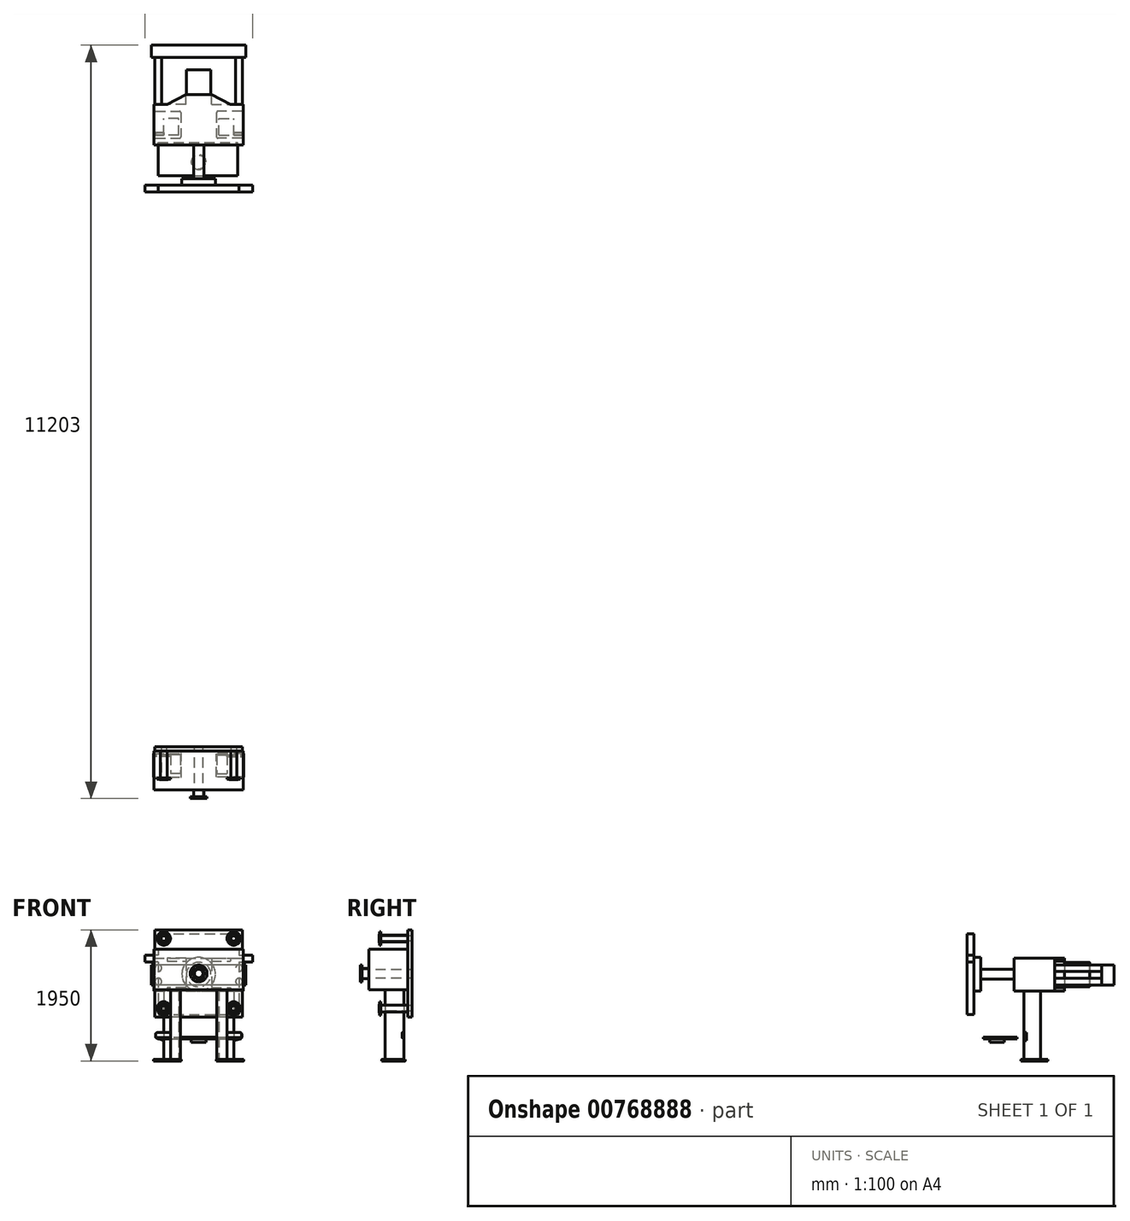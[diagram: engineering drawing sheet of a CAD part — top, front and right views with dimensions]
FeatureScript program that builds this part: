
annotation { "Feature Type Name" : "Feature", "Feature Type Description" : "" }
export const myFeature = defineFeature(function(context is Context, id is Id, definition is map)
    precondition{}
    {
        {
            var Q0;
            Q0=qCreatedBy(makeId("Top.planeOp"),FACE);
            var sketch = newSketch(context, id + "F0", { "sketchPlane" : qUnion([Q0])});
            skLineSegment(sketch, "E0.bottom", {"start": v(-645, 200) * mm, "end": v(-285, 200) * mm});
            skLineSegment(sketch, "E0.top", {"start": v(-645, -200) * mm, "end": v(-285, -200) * mm});
            skLineSegment(sketch, "E0.left", {"start": v(-665, 180) * mm, "end": v(-665, -180) * mm});
            skLineSegment(sketch, "E0.right", {"start": v(-265, 180) * mm, "end": v(-265, -180) * mm});
            skPoint(sketch, "E0.middle", {"position": v(-465, 0) * mm});
            skPoint(sketch, "E1.visualSharp", {"position": v(-665, 200) * mm});
            skArc(sketch, "E1.filletArc", {"start": v(-645, 200) * mm, "mid": v(-659.14, 194.14) * mm, "end": v(-665, 180) * mm});
            skPoint(sketch, "E2.visualSharp", {"position": v(-265, 200) * mm});
            skArc(sketch, "E2.filletArc", {"start": v(-265, 180) * mm, "mid": v(-270.86, 194.14) * mm, "end": v(-285, 200) * mm});
            skPoint(sketch, "E3.visualSharp", {"position": v(-265, -200) * mm});
            skArc(sketch, "E3.filletArc", {"start": v(-285, -200) * mm, "mid": v(-270.86, -194.14) * mm, "end": v(-265, -180) * mm});
            skPoint(sketch, "E4.visualSharp", {"position": v(-665, -200) * mm});
            skArc(sketch, "E4.filletArc", {"start": v(-665, -180) * mm, "mid": v(-659.14, -194.14) * mm, "end": v(-645, -200) * mm});
            skArc(sketch, "E5.MirrorCS", {"start": v(265, 180) * mm, "mid": v(270.86, 194.14) * mm, "end": v(285, 200) * mm});
            skArc(sketch, "E6.MirrorCS", {"start": v(285, -200) * mm, "mid": v(270.86, -194.14) * mm, "end": v(265, -180) * mm});
            skArc(sketch, "E7.MirrorCS", {"start": v(645, 200) * mm, "mid": v(659.14, 194.14) * mm, "end": v(665, 180) * mm});
            skArc(sketch, "E8.MirrorCS", {"start": v(665, -180) * mm, "mid": v(659.14, -194.14) * mm, "end": v(645, -200) * mm});
            skPoint(sketch, "E9.MirrorP", {"position": v(665, -200) * mm});
            skLineSegment(sketch, "E10.MirrorCS", {"start": v(265, 180) * mm, "end": v(265, -180) * mm});
            skPoint(sketch, "E11.MirrorP", {"position": v(665, 200) * mm});
            skPoint(sketch, "E12.MirrorP", {"position": v(265, 200) * mm});
            skLineSegment(sketch, "E13.MirrorCS", {"start": v(665, 180) * mm, "end": v(665, -180) * mm});
            skPoint(sketch, "E14.MirrorP", {"position": v(465, 0) * mm});
            skLineSegment(sketch, "E15.MirrorCS", {"start": v(645, -200) * mm, "end": v(285, -200) * mm});
            skLineSegment(sketch, "E16.MirrorCS", {"start": v(645, 200) * mm, "end": v(285, 200) * mm});
            skPoint(sketch, "E17.MirrorP", {"position": v(265, -200) * mm});
            skSolve(sketch);
        }
        {
            var Q0;
            Q0=makeQuery(id+"F0.imprint","IMPRINT",FACE,{"disambiguationData":[TD([[makeQuery(id+"F0.imprint","IMPRINT",EDGE,{"derivedFrom":sQuery(id+"F0.wireOp",EDGE,"E0.bottom")}),-1.0]])]});
            var sketch = newSketch(context, id + "F1", { "sketchPlane" : qUnion([Q0])});
            skPoint(sketch, "E18.0", {"position": v(-465, 0) * mm});
            skLineSegment(sketch, "E19.bottom", {"start": v(-665, -9700) * mm, "end": v(-265, -9700) * mm});
            skLineSegment(sketch, "E19.top", {"start": v(-665, -9350) * mm, "end": v(-265, -9350) * mm});
            skLineSegment(sketch, "E19.left", {"start": v(-670, -9695) * mm, "end": v(-670, -9355) * mm});
            skLineSegment(sketch, "E19.right", {"start": v(-260, -9695) * mm, "end": v(-260, -9355) * mm});
            skPoint(sketch, "E19.middle", {"position": v(-465, -9525) * mm});
            skPoint(sketch, "E20.visualSharp", {"position": v(-670, -9350) * mm});
            skArc(sketch, "E20.filletArc", {"start": v(-665, -9350) * mm, "mid": v(-668.54, -9351.46) * mm, "end": v(-670, -9355) * mm});
            skPoint(sketch, "E21.visualSharp", {"position": v(-670, -9700) * mm});
            skArc(sketch, "E21.filletArc", {"start": v(-670, -9695) * mm, "mid": v(-668.54, -9698.54) * mm, "end": v(-665, -9700) * mm});
            skPoint(sketch, "E22.visualSharp", {"position": v(-260, -9350) * mm});
            skArc(sketch, "E22.filletArc", {"start": v(-260, -9355) * mm, "mid": v(-261.46, -9351.46) * mm, "end": v(-265, -9350) * mm});
            skPoint(sketch, "E23.visualSharp", {"position": v(-260, -9700) * mm});
            skArc(sketch, "E23.filletArc", {"start": v(-265, -9700) * mm, "mid": v(-261.46, -9698.54) * mm, "end": v(-260, -9695) * mm});
            skArc(sketch, "E24.MirrorCS", {"start": v(260, -9355) * mm, "mid": v(261.46, -9351.46) * mm, "end": v(265, -9350) * mm});
            skArc(sketch, "E25.MirrorCS", {"start": v(670, -9695) * mm, "mid": v(668.54, -9698.54) * mm, "end": v(665, -9700) * mm});
            skArc(sketch, "E26.MirrorCS", {"start": v(265, -9700) * mm, "mid": v(261.46, -9698.54) * mm, "end": v(260, -9695) * mm});
            skArc(sketch, "E27.MirrorCS", {"start": v(665, -9350) * mm, "mid": v(668.54, -9351.46) * mm, "end": v(670, -9355) * mm});
            skLineSegment(sketch, "E28.MirrorCS", {"start": v(670, -9695) * mm, "end": v(670, -9355) * mm});
            skLineSegment(sketch, "E29.MirrorCS", {"start": v(260, -9695) * mm, "end": v(260, -9355) * mm});
            skLineSegment(sketch, "E30.MirrorCS", {"start": v(665, -9350) * mm, "end": v(265, -9350) * mm});
            skLineSegment(sketch, "E31.MirrorCS", {"start": v(665, -9700) * mm, "end": v(265, -9700) * mm});
            skPoint(sketch, "E32.MirrorP", {"position": v(670, -9350) * mm});
            skPoint(sketch, "E33.MirrorP", {"position": v(670, -9700) * mm});
            skPoint(sketch, "E34.MirrorP", {"position": v(260, -9700) * mm});
            skPoint(sketch, "E35.MirrorP", {"position": v(260, -9350) * mm});
            skPoint(sketch, "E36.MirrorP", {"position": v(465, -9525) * mm});
            skSolve(sketch);
        }
        {
            var Q0;
            Q0 = qSketchRegion(id + "F0", true);
            var Q1;
            Q1 = qSketchRegion(id + "F1", true);
            extrude(context, id + "F2", {"entities" : qUnion([Q0, Q1]), "depth" : 20 * mm, "offsetDistance" : 25 * mm});
        }
        {
            var Q0;
            Q0=makeQuery(id+"F2.opExtrude","CAP_FACE",FACE,{"disambiguationData":[OSD([sQuery(id+"F0.wireOp",EDGE,"E0.bottom"),sQuery(id+"F0.wireOp",EDGE,"E0.top"),sQuery(id+"F0.wireOp",EDGE,"E0.left"),sQuery(id+"F0.wireOp",EDGE,"E0.right"),sQuery(id+"F0.wireOp",EDGE,"E1.filletArc"),sQuery(id+"F0.wireOp",EDGE,"E2.filletArc"),sQuery(id+"F0.wireOp",EDGE,"E3.filletArc"),sQuery(id+"F0.wireOp",EDGE,"E4.filletArc")])],"isStart":false});
            var sketch = newSketch(context, id + "F3", { "sketchPlane" : qUnion([Q0])});
            skLineSegment(sketch, "E37.bottom", {"start": v(-300, -156.09) * mm, "end": v(-520, -156.09) * mm});
            skLineSegment(sketch, "E37.top", {"start": v(-300, 93.91) * mm, "end": v(-520, 93.91) * mm});
            skLineSegment(sketch, "E37.left", {"start": v(-300, -156.09) * mm, "end": v(-300, 93.91) * mm});
            skLineSegment(sketch, "E37.right", {"start": v(-520, -156.09) * mm, "end": v(-520, 93.91) * mm});
            skPoint(sketch, "E37.middle", {"position": v(-410, -31.09) * mm});
            skLineSegment(sketch, "E38.MirrorCS", {"start": v(300, -156.09) * mm, "end": v(520, -156.09) * mm});
            skLineSegment(sketch, "E39.MirrorCS", {"start": v(300, 93.91) * mm, "end": v(520, 93.91) * mm});
            skLineSegment(sketch, "E40.MirrorCS", {"start": v(520, -156.09) * mm, "end": v(520, 93.91) * mm});
            skLineSegment(sketch, "E41.MirrorCS", {"start": v(300, -156.09) * mm, "end": v(300, 93.91) * mm});
            skPoint(sketch, "E42.MirrorP", {"position": v(410, -31.09) * mm});
            skSolve(sketch);
        }
        {
            var Q0;
            Q0 = qSketchRegion(id + "F3", true);
            extrude(context, id + "F4", {"entities" : qUnion([Q0]), "operationType" : NewBodyOperationType.ADD, "depth" : 1020 * mm, "offsetDistance" : 25 * mm});
        }
        {
            var Q0;
            Q0=makeQuery(id+"F2.opExtrude","CAP_FACE",FACE,{"disambiguationData":[OSD([sQuery(id+"F1.wireOp",EDGE,"E19.bottom"),sQuery(id+"F1.wireOp",EDGE,"E19.top"),sQuery(id+"F1.wireOp",EDGE,"E19.left"),sQuery(id+"F1.wireOp",EDGE,"E19.right"),sQuery(id+"F1.wireOp",EDGE,"E20.filletArc"),sQuery(id+"F1.wireOp",EDGE,"E21.filletArc"),sQuery(id+"F1.wireOp",EDGE,"E22.filletArc"),sQuery(id+"F1.wireOp",EDGE,"E23.filletArc")])],"isStart":false});
            var sketch = newSketch(context, id + "F5", { "sketchPlane" : qUnion([Q0])});
            skLineSegment(sketch, "E43.bottom", {"start": v(-270, -9370) * mm, "end": v(-420, -9370) * mm});
            skLineSegment(sketch, "E43.top", {"start": v(-270, -9650) * mm, "end": v(-420, -9650) * mm});
            skLineSegment(sketch, "E43.left", {"start": v(-270, -9370) * mm, "end": v(-270, -9650) * mm});
            skLineSegment(sketch, "E43.right", {"start": v(-420, -9370) * mm, "end": v(-420, -9650) * mm});
            skLineSegment(sketch, "E44.MirrorCS", {"start": v(270, -9370) * mm, "end": v(420, -9370) * mm});
            skLineSegment(sketch, "E45.MirrorCS", {"start": v(420, -9370) * mm, "end": v(420, -9650) * mm});
            skLineSegment(sketch, "E46.MirrorCS", {"start": v(270, -9650) * mm, "end": v(420, -9650) * mm});
            skLineSegment(sketch, "E47.MirrorCS", {"start": v(270, -9370) * mm, "end": v(270, -9650) * mm});
            skSolve(sketch);
        }
        {
            var Q0;
            Q0 = qSketchRegion(id + "F5", true);
            extrude(context, id + "F6", {"entities" : qUnion([Q0]), "operationType" : NewBodyOperationType.ADD, "depth" : 1040 * mm, "offsetDistance" : 25 * mm});
        }
        {
            var Q0;
            Q0=makeQuery(id+"F4.opExtrude","CAP_FACE",FACE,{"disambiguationData":[OSD([sQuery(id+"F3.wireOp",EDGE,"E37.bottom"),sQuery(id+"F3.wireOp",EDGE,"E37.top"),sQuery(id+"F3.wireOp",EDGE,"E37.left"),sQuery(id+"F3.wireOp",EDGE,"E37.right")])],"isStart":false});
            var sketch = newSketch(context, id + "F7", { "sketchPlane" : qUnion([Q0])});
            skLineSegment(sketch, "E48.bottom", {"start": v(-663.5, 300) * mm, "end": v(-470, 300) * mm});
            skLineSegment(sketch, "E48.top", {"start": v(-663.5, -300) * mm, "end": v(663.5, -300) * mm});
            skLineSegment(sketch, "E48.left", {"start": v(-663.5, 300) * mm, "end": v(-663.5, -300) * mm});
            skLineSegment(sketch, "E48.right", {"start": v(663.5, 300) * mm, "end": v(663.5, -300) * mm});
            skLineSegment(sketch, "E49", {"start": v(-190, 450) * mm, "end": v(190, 450) * mm});
            skLineSegment(sketch, "E50", {"start": v(-190, 450) * mm, "end": v(-470, 300) * mm});
            skLineSegment(sketch, "E51", {"start": v(190, 450) * mm, "end": v(470, 300) * mm});
            skLineSegment(sketch, "E52.trimOffspring", {"start": v(470, 300) * mm, "end": v(663.5, 300) * mm});
            skSolve(sketch);
        }
        {
            var Q0;
            Q0=makeQuery(id+"F7.imprint","IMPRINT",FACE,{"disambiguationData":[TD([[makeQuery(id+"F7.imprint","IMPRINT",EDGE,{"derivedFrom":sQuery(id+"F7.wireOp",EDGE,"E48.bottom")}),-1.0]])]});
            var Q1;
            Q1=makeQuery(id+"F7.imprint","IMPRINT",FACE,{"disambiguationData":[TD([[makeQuery(id+"F7.imprint","IMPRINT",EDGE,{"derivedFrom":makeQuery(id+"F4.opExtrude","CAP_EDGE",EDGE,{"disambiguationData":[OSD([sQuery(id+"F3.wireOp",EDGE,"E37.bottom")])],"isStart":false})}),-1.0]])]});
            extrude(context, id + "F8", {"entities" : qUnion([Q0, Q1]), "operationType" : NewBodyOperationType.ADD, "depth" : 490 * mm, "offsetDistance" : 25 * mm});
        }
        {
            var Q0;
            Q0=makeQuery(id+"F6.opExtrude","CAP_FACE",FACE,{"disambiguationData":[OSD([sQuery(id+"F5.wireOp",EDGE,"E43.bottom"),sQuery(id+"F5.wireOp",EDGE,"E43.top"),sQuery(id+"F5.wireOp",EDGE,"E43.left"),sQuery(id+"F5.wireOp",EDGE,"E43.right")])],"isStart":false});
            var sketch = newSketch(context, id + "F9", { "sketchPlane" : qUnion([Q0])});
            skLineSegment(sketch, "E53.bottom", {"start": v(-663.5, -9310) * mm, "end": v(663.5, -9310) * mm});
            skLineSegment(sketch, "E53.top", {"start": v(-663.5, -9889) * mm, "end": v(663.5, -9889) * mm});
            skLineSegment(sketch, "E53.left", {"start": v(-663.5, -9310) * mm, "end": v(-663.5, -9889) * mm});
            skLineSegment(sketch, "E53.right", {"start": v(663.5, -9310) * mm, "end": v(663.5, -9889) * mm});
            skSolve(sketch);
        }
        {
            var Q0;
            Q0=makeQuery(id+"F9.imprint","IMPRINT",FACE,{"disambiguationData":[TD([[makeQuery(id+"F9.imprint","IMPRINT",EDGE,{"derivedFrom":sQuery(id+"F9.wireOp",EDGE,"E53.bottom")}),-1.0]])]});
            var Q1;
            Q1=makeQuery(id+"F9.imprint","IMPRINT",FACE,{"disambiguationData":[TD([[makeQuery(id+"F9.imprint","IMPRINT",EDGE,{"derivedFrom":makeQuery(id+"F6.opExtrude","CAP_EDGE",EDGE,{"disambiguationData":[OSD([sQuery(id+"F5.wireOp",EDGE,"E43.bottom")])],"isStart":false})}),1.0]])]});
            extrude(context, id + "F10", {"entities" : qUnion([Q0, Q1]), "operationType" : NewBodyOperationType.ADD, "depth" : 600 * mm, "offsetDistance" : 25 * mm});
        }
        {
            var Q0;
            Q0=makeQuery(id+"F8.opExtrude","SWEPT_FACE",FACE,{"disambiguationData":[OSD([sQuery(id+"F7.wireOp",EDGE,"E49")])]});
            var sketch = newSketch(context, id + "F11", { "sketchPlane" : qUnion([Q0])});
            skCircle(sketch, "E54", {"center": v(0, 1285) * mm, "radius": 182 * mm});
            skSolve(sketch);
        }
        {
            var Q0;
            Q0=makeQuery(id+"F11.imprint","IMPRINT",FACE,{"disambiguationData":[TD([[makeQuery(id+"F11.imprint","IMPRINT",EDGE,{"derivedFrom":sQuery(id+"F11.wireOp",EDGE,"E54")}),1.0]])]});
            extrude(context, id + "F12", {"entities" : qUnion([Q0]), "operationType" : NewBodyOperationType.ADD, "depth" : 370 * mm, "offsetDistance" : 25 * mm});
        }
        {
            var Q0;
            Q0=makeQuery(id+"F8.opExtrude","SWEPT_FACE",FACE,{"disambiguationData":[OSD([sQuery(id+"F7.wireOp",EDGE,"E49")])]});
            var sketch = newSketch(context, id + "F13", { "sketchPlane" : qUnion([Q0])});
            skLineSegment(sketch, "E55.bottom", {"start": v(-190, 1484.67) * mm, "end": v(-470, 1484.67) * mm});
            skLineSegment(sketch, "E55.top", {"start": v(-190, 1087.5) * mm, "end": v(-470, 1087.5) * mm});
            skLineSegment(sketch, "E55.left", {"start": v(-190, 1484.67) * mm, "end": v(-190, 1087.5) * mm});
            skLineSegment(sketch, "E55.right", {"start": v(-470, 1484.67) * mm, "end": v(-470, 1087.5) * mm});
            skLineSegment(sketch, "E56.bottom", {"start": v(190, 1484.67) * mm, "end": v(470, 1484.67) * mm});
            skLineSegment(sketch, "E56.top", {"start": v(190, 1087.5) * mm, "end": v(470, 1087.5) * mm});
            skLineSegment(sketch, "E56.left", {"start": v(190, 1484.67) * mm, "end": v(190, 1087.5) * mm});
            skLineSegment(sketch, "E56.right", {"start": v(470, 1484.67) * mm, "end": v(470, 1087.5) * mm});
            skSolve(sketch);
        }
        {
            var Q0;
            Q0=makeQuery(id+"F13.imprint","IMPRINT",FACE,{"disambiguationData":[TD([[makeQuery(id+"F13.imprint","IMPRINT",EDGE,{"derivedFrom":sQuery(id+"F13.wireOp",EDGE,"E55.bottom")}),1.0]])]});
            var Q1;
            Q1=makeQuery(id+"F13.imprint","IMPRINT",FACE,{"disambiguationData":[TD([[makeQuery(id+"F13.imprint","IMPRINT",EDGE,{"derivedFrom":sQuery(id+"F13.wireOp",EDGE,"E56.bottom")}),-1.0]])]});
            extrude(context, id + "F14", {"entities" : qUnion([Q0, Q1]), "operationType" : NewBodyOperationType.REMOVE, "oppositeDirection" : true, "depth" : 150 * mm, "offsetDistance" : 25 * mm});
        }
        {
            var Q0;
            Q0=makeQuery(id+"F10.opExtrude","SWEPT_FACE",FACE,{"disambiguationData":[OSD([sQuery(id+"F9.wireOp",EDGE,"E53.bottom")])]});
            var sketch = newSketch(context, id + "F15", { "sketchPlane" : qUnion([Q0])});
            skLineSegment(sketch, "E57.bottom", {"start": v(-650, 1950) * mm, "end": v(650, 1950) * mm});
            skLineSegment(sketch, "E57.top", {"start": v(-650, 650) * mm, "end": v(650, 650) * mm});
            skLineSegment(sketch, "E57.left", {"start": v(-650, 1950) * mm, "end": v(-650, 650) * mm});
            skLineSegment(sketch, "E57.right", {"start": v(650, 1950) * mm, "end": v(650, 650) * mm});
            skSolve(sketch);
        }
        {
            var Q0;
            Q0 = qSketchRegion(id + "F15", true);
            extrude(context, id + "F16", {"entities" : qUnion([Q0]), "operationType" : NewBodyOperationType.ADD, "depth" : 60 * mm, "offsetDistance" : 25 * mm});
        }
        {
            var Q0;
            Q0=makeQuery(id+"F8.opExtrude","SWEPT_FACE",FACE,{"disambiguationData":[OSD([sQuery(id+"F7.wireOp",EDGE,"E48.top")])]});
            var sketch = newSketch(context, id + "F17", { "sketchPlane" : qUnion([Q0])});
            skCircle(sketch, "E58", {"center": v(0, 1290) * mm, "radius": 75 * mm});
            skSolve(sketch);
        }
        {
            var Q0;
            Q0=makeQuery(id+"F17.imprint","IMPRINT",FACE,{"disambiguationData":[TD([[makeQuery(id+"F17.imprint","IMPRINT",EDGE,{"derivedFrom":sQuery(id+"F17.wireOp",EDGE,"E58")}),1.0]])]});
            extrude(context, id + "F18", {"entities" : qUnion([Q0]), "depth" : 600 * mm, "offsetDistance" : 25 * mm});
        }
        {
            var Q0;
            Q0=makeQuery(id+"F18.opExtrude","CAP_FACE",FACE,{"disambiguationData":[OSD([sQuery(id+"F17.wireOp",EDGE,"E58")])],"isStart":false});
            var sketch = newSketch(context, id + "F19", { "sketchPlane" : qUnion([Q0])});
            skLineSegment(sketch, "E59.bottom", {"start": v(-600, 1890) * mm, "end": v(600, 1890) * mm});
            skLineSegment(sketch, "E59.top", {"start": v(-600, 690) * mm, "end": v(600, 690) * mm});
            skLineSegment(sketch, "E59.left", {"start": v(-600, 1890) * mm, "end": v(-600, 1570) * mm});
            skLineSegment(sketch, "E59.right", {"start": v(600, 1890) * mm, "end": v(600, 1570) * mm});
            skPoint(sketch, "E59.middle", {"position": v(0, 1290) * mm});
            skLineSegment(sketch, "E60.bottom", {"start": v(-600, 1570) * mm, "end": v(-800, 1570) * mm});
            skLineSegment(sketch, "E60.top", {"start": v(-600, 1470) * mm, "end": v(-800, 1470) * mm});
            skLineSegment(sketch, "E60.right", {"start": v(-800, 1570) * mm, "end": v(-800, 1470) * mm});
            skLineSegment(sketch, "E61.bottom", {"start": v(600, 1470) * mm, "end": v(800, 1470) * mm});
            skLineSegment(sketch, "E61.top", {"start": v(600, 1570) * mm, "end": v(800, 1570) * mm});
            skLineSegment(sketch, "E61.right", {"start": v(800, 1470) * mm, "end": v(800, 1570) * mm});
            skLineSegment(sketch, "E62.trimOffspring", {"start": v(-600, 1470) * mm, "end": v(-600, 690) * mm});
            skLineSegment(sketch, "E63.trimOffspring", {"start": v(600, 1470) * mm, "end": v(600, 690) * mm});
            skSolve(sketch);
        }
        {
            var Q0;
            Q0=makeQuery(id+"F19.imprint","IMPRINT",FACE,{"disambiguationData":[TD([[makeQuery(id+"F19.imprint","IMPRINT",EDGE,{"derivedFrom":sQuery(id+"F19.wireOp",EDGE,"E59.bottom")}),-1.0]])]});
            var Q1;
            Q1=makeQuery(id+"F19.imprint","IMPRINT",FACE,{"disambiguationData":[TD([[makeQuery(id+"F19.imprint","IMPRINT",EDGE,{"derivedFrom":makeQuery(id+"F18.opExtrude","CAP_EDGE",EDGE,{"disambiguationData":[OSD([sQuery(id+"F17.wireOp",EDGE,"E58")])],"isStart":false})}),1.0]])]});
            extrude(context, id + "F20", {"entities" : qUnion([Q0, Q1]), "operationType" : NewBodyOperationType.ADD, "depth" : 100 * mm, "offsetDistance" : 25 * mm});
        }
        {
            var Q0;
            Q0=makeQuery(id+"F20.opExtrude","CAP_FACE",FACE,{"disambiguationData":[OSD([sQuery(id+"F19.wireOp",EDGE,"E59.bottom"),sQuery(id+"F19.wireOp",EDGE,"E59.top"),sQuery(id+"F19.wireOp",EDGE,"E59.left"),sQuery(id+"F19.wireOp",EDGE,"E59.right"),sQuery(id+"F19.wireOp",EDGE,"E60.bottom"),sQuery(id+"F19.wireOp",EDGE,"E60.top"),sQuery(id+"F19.wireOp",EDGE,"E60.right"),sQuery(id+"F19.wireOp",EDGE,"E61.bottom"),sQuery(id+"F19.wireOp",EDGE,"E61.top"),sQuery(id+"F19.wireOp",EDGE,"E61.right"),sQuery(id+"F19.wireOp",EDGE,"E62.trimOffspring"),sQuery(id+"F19.wireOp",EDGE,"E63.trimOffspring")])],"isStart":true});
            var sketch = newSketch(context, id + "F21", { "sketchPlane" : qUnion([Q0])});
            skCircle(sketch, "E64", {"center": v(0, 1290) * mm, "radius": 250 * mm});
            skSolve(sketch);
        }
        {
            var Q0;
            Q0=makeQuery(id+"F21.imprint","IMPRINT",FACE,{"disambiguationData":[TD([[makeQuery(id+"F21.imprint","IMPRINT",EDGE,{"derivedFrom":sQuery(id+"F21.wireOp",EDGE,"E64")}),1.0]])]});
            extrude(context, id + "F22", {"entities" : qUnion([Q0]), "operationType" : NewBodyOperationType.ADD, "depth" : 100 * mm, "offsetDistance" : 25 * mm});
        }
        {
            var Q0;
            {var subQ0=sQuery(id+"F15.wireOp",EDGE,"E57.left");var subQ1=sQuery(id+"F15.wireOp",EDGE,"E57.bottom");var subQ3=sQuery(id+"F15.wireOp",EDGE,"E57.right");Q0=makeQuery(id+"F16.boolean.opBoolean","SPLIT",FACE,{"disambiguationData":[TD([makeQuery(id+"F16.opExtrude","SWEPT_FACE",FACE,{"disambiguationData":[OSD([subQ1])]})])],"derivedFrom":makeQuery(id+"F16.opExtrude","CAP_FACE",FACE,{"disambiguationData":[OSD([subQ1,sQuery(id+"F15.wireOp",EDGE,"E57.top"),subQ0,subQ3])],"isStart":true})});}
            var sketch = newSketch(context, id + "F23", { "sketchPlane" : qUnion([Q0])});
            skCircle(sketch, "E65", {"center": v(-520, 1820) * mm, "radius": 40 * mm});
            skCircle(sketch, "E66", {"center": v(520, 1820) * mm, "radius": 40 * mm});
            skSolve(sketch);
        }
        {
            var Q0;
            Q0 = qSketchRegion(id + "F23", true);
            extrude(context, id + "F24", {"entities" : qUnion([Q0]), "operationType" : NewBodyOperationType.REMOVE, "oppositeDirection" : true, "depth" : 60 * mm, "offsetDistance" : 25 * mm});
        }
        {
            var Q0;
            {var subQ0=sQuery(id+"F15.wireOp",EDGE,"E57.left");var subQ1=sQuery(id+"F15.wireOp",EDGE,"E57.bottom");var subQ3=sQuery(id+"F15.wireOp",EDGE,"E57.right");Q0=makeQuery(id+"F16.boolean.opBoolean","SPLIT",FACE,{"disambiguationData":[TD([makeQuery(id+"F16.opExtrude","SWEPT_FACE",FACE,{"disambiguationData":[OSD([subQ1])]})])],"derivedFrom":makeQuery(id+"F16.opExtrude","CAP_FACE",FACE,{"disambiguationData":[OSD([subQ1,sQuery(id+"F15.wireOp",EDGE,"E57.top"),subQ0,subQ3])],"isStart":true})});}
            var sketch = newSketch(context, id + "F25", { "sketchPlane" : qUnion([Q0])});
            skCircle(sketch, "E67", {"center": v(-520, 1820) * mm, "radius": 50 * mm});
            skCircle(sketch, "E68", {"center": v(-520, 1820) * mm, "radius": 100 * mm});
            skCircle(sketch, "E69", {"center": v(-440, 1820) * mm, "radius": 9 * mm});
            skCircle(sketch, "E70.1.0", {"center": v(-463.43, 1876.57) * mm, "radius": 9 * mm});
            skCircle(sketch, "E70.2.0", {"center": v(-520, 1900) * mm, "radius": 9 * mm});
            skCircle(sketch, "E70.3.0", {"center": v(-576.57, 1876.57) * mm, "radius": 9 * mm});
            skCircle(sketch, "E70.4.0", {"center": v(-600, 1820) * mm, "radius": 9 * mm});
            skCircle(sketch, "E70.5.0", {"center": v(-576.57, 1763.43) * mm, "radius": 9 * mm});
            skCircle(sketch, "E70.6.0", {"center": v(-520, 1740) * mm, "radius": 9 * mm});
            skCircle(sketch, "E70.7.0", {"center": v(-463.43, 1763.43) * mm, "radius": 9 * mm});
            skSolve(sketch);
        }
        {
            var Q0;
            Q0=makeQuery(id+"F25.imprint","IMPRINT",FACE,{"disambiguationData":[TD([[makeQuery(id+"F25.imprint","IMPRINT",EDGE,{"derivedFrom":sQuery(id+"F25.wireOp",EDGE,"E67")}),1.0]])]});
            extrude(context, id + "F26", {"entities" : qUnion([Q0]), "operationType" : NewBodyOperationType.ADD, "depth" : 420 * mm, "offsetDistance" : 25 * mm});
        }
        {
            var Q0;
            Q0=makeQuery(id+"F26.opExtrude","CAP_FACE",FACE,{"disambiguationData":[OSD([sQuery(id+"F23.wireOp",EDGE,"E65"),sQuery(id+"F25.wireOp",EDGE,"E67")])],"isStart":false});
            var sketch = newSketch(context, id + "F27", { "sketchPlane" : qUnion([Q0])});
            skCircle(sketch, "E71.0", {"center": v(-520, 1900) * mm, "radius": 9 * mm});
            skCircle(sketch, "E71.1", {"center": v(-576.57, 1876.57) * mm, "radius": 9 * mm});
            skCircle(sketch, "E72.0", {"center": v(-463.43, 1763.43) * mm, "radius": 9 * mm});
            skCircle(sketch, "E72.1", {"center": v(-520, 1820) * mm, "radius": 50 * mm});
            skCircle(sketch, "E72.2", {"center": v(-520, 1820) * mm, "radius": 100 * mm});
            skCircle(sketch, "E72.3", {"center": v(-440, 1820) * mm, "radius": 9 * mm});
            skCircle(sketch, "E72.4", {"center": v(-463.43, 1876.57) * mm, "radius": 9 * mm});
            skCircle(sketch, "E72.7", {"center": v(-576.57, 1763.43) * mm, "radius": 9 * mm});
            skCircle(sketch, "E72.8", {"center": v(-520, 1820) * mm, "radius": 50 * mm});
            skCircle(sketch, "E72.9", {"center": v(-520, 1820) * mm, "radius": 40 * mm});
            skLineSegment(sketch, "E72.10", {"start": v(-663.5, 1530) * mm, "end": v(-663.5, 1040) * mm});
            skCircle(sketch, "E73.4", {"center": v(-600, 1820) * mm, "radius": 9 * mm});
            skCircle(sketch, "E73.6", {"center": v(-520, 1740) * mm, "radius": 9 * mm});
            skSolve(sketch);
        }
        {
            var Q0;
            Q0=makeQuery(id+"F27.imprint","IMPRINT",FACE,{"disambiguationData":[TD([[makeQuery(id+"F27.imprint","IMPRINT",EDGE,{"derivedFrom":sQuery(id+"F27.wireOp",EDGE,"E72.4")}),-1.0]])]});
            extrude(context, id + "F28", {"entities" : qUnion([Q0]), "operationType" : NewBodyOperationType.ADD, "oppositeDirection" : true, "depth" : 20 * mm, "offsetDistance" : 25 * mm});
        }
        {
            var Q0;
            Q0=makeQuery(id+"F28.boolean.opBoolean","MERGE",FACE,{"derivedFrom":[makeQuery(id+"F26.opExtrude","CAP_FACE",FACE,{"disambiguationData":[OSD([sQuery(id+"F23.wireOp",EDGE,"E65"),sQuery(id+"F25.wireOp",EDGE,"E67")])],"isStart":false}),makeQuery(id+"F28.opExtrude","CAP_FACE",FACE,{"disambiguationData":[OSD([sQuery(id+"F27.wireOp",EDGE,"E72.4"),sQuery(id+"F27.wireOp",EDGE,"E71.0"),sQuery(id+"F27.wireOp",EDGE,"E71.1"),sQuery(id+"F27.wireOp",EDGE,"E72.0"),sQuery(id+"F27.wireOp",EDGE,"E72.1"),sQuery(id+"F27.wireOp",EDGE,"E72.2"),sQuery(id+"F27.wireOp",EDGE,"E72.3"),sQuery(id+"F27.wireOp",EDGE,"E73.4"),sQuery(id+"F27.wireOp",EDGE,"E72.7"),sQuery(id+"F27.wireOp",EDGE,"E73.6")])],"isStart":true})]});
            var sketch = newSketch(context, id + "F29", { "sketchPlane" : qUnion([Q0])});
            skCircle(sketch, "E74", {"center": v(-520, 1820) * mm, "radius": 65 * mm});
            skSolve(sketch);
        }
        {
            var Q0;
            Q0=makeQuery(id+"F29.imprint","IMPRINT",FACE,{"disambiguationData":[TD([[makeQuery(id+"F29.imprint","IMPRINT",EDGE,{"derivedFrom":sQuery(id+"F29.wireOp",EDGE,"E74")}),1.0]])]});
            extrude(context, id + "F30", {"entities" : qUnion([Q0]), "operationType" : NewBodyOperationType.ADD, "depth" : 5 * mm, "offsetDistance" : 25 * mm});
        }
        {
            var Q0;
            Q0=makeQuery(id+"F25.imprint","IMPRINT",FACE,{"disambiguationData":[TD([[makeQuery(id+"F25.imprint","IMPRINT",EDGE,{"derivedFrom":sQuery(id+"F25.wireOp",EDGE,"E68")}),-1.0]])]});
            var sketch = newSketch(context, id + "F31", { "sketchPlane" : qUnion([Q0])});
            skCircle(sketch, "E75.0", {"center": v(520, 1820) * mm, "radius": 40 * mm});
            skCircle(sketch, "E76", {"center": v(520, 1820) * mm, "radius": 45 * mm});
            skCircle(sketch, "E77", {"center": v(520, 1820) * mm, "radius": 100 * mm});
            skCircle(sketch, "E78", {"center": v(600, 1820) * mm, "radius": 9 * mm});
            skCircle(sketch, "E79.1.0", {"center": v(576.57, 1876.57) * mm, "radius": 9 * mm});
            skCircle(sketch, "E79.2.0", {"center": v(520, 1900) * mm, "radius": 9 * mm});
            skCircle(sketch, "E79.3.0", {"center": v(463.43, 1876.57) * mm, "radius": 9 * mm});
            skCircle(sketch, "E79.4.0", {"center": v(440, 1820) * mm, "radius": 9 * mm});
            skCircle(sketch, "E79.5.0", {"center": v(463.43, 1763.43) * mm, "radius": 9 * mm});
            skCircle(sketch, "E79.6.0", {"center": v(520, 1740) * mm, "radius": 9 * mm});
            skCircle(sketch, "E79.7.0", {"center": v(576.57, 1763.43) * mm, "radius": 9 * mm});
            skSolve(sketch);
        }
        {
            var Q0;
            Q0=makeQuery(id+"F31.imprint","IMPRINT",FACE,{"disambiguationData":[TD([[makeQuery(id+"F31.imprint","IMPRINT",EDGE,{"derivedFrom":sQuery(id+"F31.wireOp",EDGE,"E75.0")}),-1.0]])]});
            extrude(context, id + "F32", {"entities" : qUnion([Q0]), "operationType" : NewBodyOperationType.ADD, "depth" : 420 * mm, "offsetDistance" : 25 * mm});
        }
        {
            var Q0;
            Q0=makeQuery(id+"F32.opExtrude","CAP_FACE",FACE,{"disambiguationData":[OSD([sQuery(id+"F31.wireOp",EDGE,"E75.0"),sQuery(id+"F31.wireOp",EDGE,"E76")])],"isStart":false});
            var sketch = newSketch(context, id + "F33", { "sketchPlane" : qUnion([Q0])});
            skCircle(sketch, "E80.0", {"center": v(520, 1820) * mm, "radius": 40 * mm});
            skCircle(sketch, "E80.1", {"center": v(520, 1820) * mm, "radius": 45 * mm});
            skCircle(sketch, "E80.2", {"center": v(600, 1820) * mm, "radius": 9 * mm});
            skCircle(sketch, "E80.3", {"center": v(576.57, 1763.43) * mm, "radius": 9 * mm});
            skCircle(sketch, "E80.4", {"center": v(520, 1900) * mm, "radius": 9 * mm});
            skCircle(sketch, "E80.5", {"center": v(576.57, 1876.57) * mm, "radius": 9 * mm});
            skCircle(sketch, "E80.6", {"center": v(463.43, 1876.57) * mm, "radius": 9 * mm});
            skCircle(sketch, "E80.7", {"center": v(440, 1820) * mm, "radius": 9 * mm});
            skCircle(sketch, "E80.8", {"center": v(520, 1740) * mm, "radius": 9 * mm});
            skCircle(sketch, "E80.9", {"center": v(463.43, 1763.43) * mm, "radius": 9 * mm});
            skCircle(sketch, "E81.0", {"center": v(520, 1820) * mm, "radius": 100 * mm});
            skSolve(sketch);
        }
        {
            var Q0;
            Q0 = qSketchRegion(id + "F33", true);
            var Q1;
            Q1=makeQuery(id+"F33.imprint","IMPRINT",FACE,{"disambiguationData":[TD([[makeQuery(id+"F33.imprint","IMPRINT",EDGE,{"derivedFrom":sQuery(id+"F33.wireOp",EDGE,"E80.0")}),-1.0]])]});
            extrude(context, id + "F34", {"entities" : qUnion([Q0, Q1]), "operationType" : NewBodyOperationType.ADD, "oppositeDirection" : true, "depth" : 20 * mm, "offsetDistance" : 25 * mm});
        }
        {
            var Q0;
            Q0=makeQuery(id+"F34.boolean.opBoolean","MERGE",FACE,{"derivedFrom":[makeQuery(id+"F32.opExtrude","CAP_FACE",FACE,{"disambiguationData":[OSD([sQuery(id+"F31.wireOp",EDGE,"E75.0"),sQuery(id+"F31.wireOp",EDGE,"E76")])],"isStart":false}),makeQuery(id+"F34.opExtrude","CAP_FACE",FACE,{"disambiguationData":[OSD([sQuery(id+"F33.wireOp",EDGE,"E80.0"),sQuery(id+"F33.wireOp",EDGE,"E80.2"),sQuery(id+"F33.wireOp",EDGE,"E80.3"),sQuery(id+"F33.wireOp",EDGE,"E80.4"),sQuery(id+"F33.wireOp",EDGE,"E80.5"),sQuery(id+"F33.wireOp",EDGE,"E80.6"),sQuery(id+"F33.wireOp",EDGE,"E80.7"),sQuery(id+"F33.wireOp",EDGE,"E80.8"),sQuery(id+"F33.wireOp",EDGE,"E80.9"),sQuery(id+"F33.wireOp",EDGE,"E81.0")])],"isStart":true})]});
            var sketch = newSketch(context, id + "F35", { "sketchPlane" : qUnion([Q0])});
            skCircle(sketch, "E82", {"center": v(520, 1820) * mm, "radius": 65 * mm});
            skSolve(sketch);
        }
        {
            var Q0;
            Q0=makeQuery(id+"F35.imprint","IMPRINT",FACE,{"disambiguationData":[TD([[makeQuery(id+"F35.imprint","IMPRINT",EDGE,{"derivedFrom":sQuery(id+"F35.wireOp",EDGE,"E82")}),1.0]])]});
            extrude(context, id + "F36", {"entities" : qUnion([Q0]), "operationType" : NewBodyOperationType.ADD, "depth" : 5 * mm, "offsetDistance" : 25 * mm});
        }
        {
            var Q0;
            {var subQ0=sQuery(id+"F15.wireOp",EDGE,"E57.left");var subQ2=sQuery(id+"F15.wireOp",EDGE,"E57.top");var subQ3=sQuery(id+"F15.wireOp",EDGE,"E57.right");Q0=makeQuery(id+"F16.boolean.opBoolean","SPLIT",FACE,{"disambiguationData":[TD([makeQuery(id+"F16.opExtrude","SWEPT_FACE",FACE,{"disambiguationData":[OSD([subQ2])]})])],"derivedFrom":makeQuery(id+"F16.opExtrude","CAP_FACE",FACE,{"disambiguationData":[OSD([sQuery(id+"F15.wireOp",EDGE,"E57.bottom"),subQ2,subQ0,subQ3])],"isStart":true})});}
            var sketch = newSketch(context, id + "F37", { "sketchPlane" : qUnion([Q0])});
            skPoint(sketch, "E83.0", {"position": v(-520, 1820) * mm});
            skCircle(sketch, "E84", {"center": v(-520, 780) * mm, "radius": 40 * mm});
            skCircle(sketch, "E85", {"center": v(520, 780) * mm, "radius": 40 * mm});
            skSolve(sketch);
        }
        {
            var Q0;
            Q0 = qSketchRegion(id + "F37", true);
            extrude(context, id + "F38", {"entities" : qUnion([Q0]), "operationType" : NewBodyOperationType.REMOVE, "oppositeDirection" : true, "depth" : 100 * mm, "offsetDistance" : 25 * mm});
        }
        {
            var Q0;
            {var subQ0=sQuery(id+"F15.wireOp",EDGE,"E57.left");var subQ2=sQuery(id+"F15.wireOp",EDGE,"E57.top");var subQ3=sQuery(id+"F15.wireOp",EDGE,"E57.right");Q0=makeQuery(id+"F16.boolean.opBoolean","SPLIT",FACE,{"disambiguationData":[TD([makeQuery(id+"F16.opExtrude","SWEPT_FACE",FACE,{"disambiguationData":[OSD([subQ2])]})])],"derivedFrom":makeQuery(id+"F16.opExtrude","CAP_FACE",FACE,{"disambiguationData":[OSD([sQuery(id+"F15.wireOp",EDGE,"E57.bottom"),subQ2,subQ0,subQ3])],"isStart":true})});}
            var sketch = newSketch(context, id + "F39", { "sketchPlane" : qUnion([Q0])});
            skCircle(sketch, "E86", {"center": v(-520, 780) * mm, "radius": 50 * mm});
            skCircle(sketch, "E87", {"center": v(520, 780) * mm, "radius": 50 * mm});
            skSolve(sketch);
        }
        {
            var Q0;
            Q0=makeQuery(id+"F39.imprint","IMPRINT",FACE,{"disambiguationData":[TD([[makeQuery(id+"F39.imprint","IMPRINT",EDGE,{"derivedFrom":sQuery(id+"F39.wireOp",EDGE,"E86")}),1.0]])]});
            var Q1;
            Q1=makeQuery(id+"F39.imprint","IMPRINT",FACE,{"disambiguationData":[TD([[makeQuery(id+"F39.imprint","IMPRINT",EDGE,{"derivedFrom":sQuery(id+"F39.wireOp",EDGE,"E87")}),1.0]])]});
            extrude(context, id + "F40", {"entities" : qUnion([Q0, Q1]), "operationType" : NewBodyOperationType.ADD, "depth" : 400 * mm, "offsetDistance" : 25 * mm});
        }
        {
            var Q0;
            Q0=makeQuery(id+"F40.opExtrude","CAP_FACE",FACE,{"disambiguationData":[OSD([sQuery(id+"F37.wireOp",EDGE,"E84"),sQuery(id+"F39.wireOp",EDGE,"E86")])],"isStart":false});
            var sketch = newSketch(context, id + "F41", { "sketchPlane" : qUnion([Q0])});
            skCircle(sketch, "E88", {"center": v(-520, 780) * mm, "radius": 100 * mm});
            skCircle(sketch, "E89.0", {"center": v(520, 780) * mm, "radius": 40 * mm});
            skCircle(sketch, "E90", {"center": v(520, 780) * mm, "radius": 100 * mm});
            skCircle(sketch, "E91", {"center": v(-520, 860) * mm, "radius": 9 * mm});
            skCircle(sketch, "E92.1.0", {"center": v(-576.57, 836.57) * mm, "radius": 9 * mm});
            skCircle(sketch, "E92.2.0", {"center": v(-600, 780) * mm, "radius": 9 * mm});
            skCircle(sketch, "E92.3.0", {"center": v(-576.57, 723.43) * mm, "radius": 9 * mm});
            skCircle(sketch, "E92.4.0", {"center": v(-520, 700) * mm, "radius": 9 * mm});
            skCircle(sketch, "E92.5.0", {"center": v(-463.43, 723.43) * mm, "radius": 9 * mm});
            skCircle(sketch, "E92.6.0", {"center": v(-440, 780) * mm, "radius": 9 * mm});
            skCircle(sketch, "E92.7.0", {"center": v(-463.43, 836.57) * mm, "radius": 9 * mm});
            skCircle(sketch, "E93", {"center": v(520, 860) * mm, "radius": 9 * mm});
            skCircle(sketch, "E94.1.0", {"center": v(463.43, 836.57) * mm, "radius": 9 * mm});
            skCircle(sketch, "E94.2.0", {"center": v(440, 780) * mm, "radius": 9 * mm});
            skCircle(sketch, "E94.3.0", {"center": v(463.43, 723.43) * mm, "radius": 9 * mm});
            skCircle(sketch, "E94.4.0", {"center": v(520, 700) * mm, "radius": 9 * mm});
            skCircle(sketch, "E94.5.0", {"center": v(576.57, 723.43) * mm, "radius": 9 * mm});
            skCircle(sketch, "E94.6.0", {"center": v(600, 780) * mm, "radius": 9 * mm});
            skCircle(sketch, "E94.7.0", {"center": v(576.57, 836.57) * mm, "radius": 9 * mm});
            skSolve(sketch);
        }
        {
            var Q0;
            Q0=makeQuery(id+"F41.imprint","IMPRINT",FACE,{"disambiguationData":[TD([[makeQuery(id+"F41.imprint","IMPRINT",EDGE,{"derivedFrom":sQuery(id+"F41.wireOp",EDGE,"E88")}),1.0]])]});
            var Q1;
            Q1=makeQuery(id+"F41.imprint","IMPRINT",FACE,{"disambiguationData":[TD([[makeQuery(id+"F41.imprint","IMPRINT",EDGE,{"derivedFrom":makeQuery(id+"F40.opExtrude","CAP_EDGE",EDGE,{"disambiguationData":[OSD([sQuery(id+"F39.wireOp",EDGE,"E86")])],"isStart":false})}),1.0]])]});
            var Q2;
            Q2=makeQuery(id+"F41.imprint","IMPRINT",FACE,{"disambiguationData":[TD([[makeQuery(id+"F41.imprint","IMPRINT",EDGE,{"derivedFrom":sQuery(id+"F41.wireOp",EDGE,"E89.0")}),-1.0]])]});
            extrude(context, id + "F42", {"entities" : qUnion([Q0, Q1, Q2]), "operationType" : NewBodyOperationType.ADD, "depth" : 20 * mm, "offsetDistance" : 25 * mm});
        }
        {
            var Q0;
            Q0=makeQuery(id+"F42.opExtrude","CAP_FACE",FACE,{"disambiguationData":[OSD([sQuery(id+"F37.wireOp",EDGE,"E84"),sQuery(id+"F41.wireOp",EDGE,"E88"),sQuery(id+"F41.wireOp",EDGE,"E91"),sQuery(id+"F41.wireOp",EDGE,"E92.1.0"),sQuery(id+"F41.wireOp",EDGE,"E92.2.0"),sQuery(id+"F41.wireOp",EDGE,"E92.3.0"),sQuery(id+"F41.wireOp",EDGE,"E92.4.0"),sQuery(id+"F41.wireOp",EDGE,"E92.5.0"),sQuery(id+"F41.wireOp",EDGE,"E92.6.0"),sQuery(id+"F41.wireOp",EDGE,"E92.7.0")])],"isStart":false});
            var sketch = newSketch(context, id + "F43", { "sketchPlane" : qUnion([Q0])});
            skCircle(sketch, "E95", {"center": v(-520, 780) * mm, "radius": 65 * mm});
            skCircle(sketch, "E96.0", {"center": v(520, 780) * mm, "radius": 40 * mm});
            skCircle(sketch, "E97", {"center": v(520, 780) * mm, "radius": 65 * mm});
            skSolve(sketch);
        }
        {
            var Q0;
            Q0=makeQuery(id+"F43.imprint","IMPRINT",FACE,{"disambiguationData":[TD([[makeQuery(id+"F43.imprint","IMPRINT",EDGE,{"derivedFrom":sQuery(id+"F43.wireOp",EDGE,"E95")}),1.0]])]});
            var Q1;
            Q1=makeQuery(id+"F43.imprint","IMPRINT",FACE,{"disambiguationData":[TD([[makeQuery(id+"F43.imprint","IMPRINT",EDGE,{"derivedFrom":sQuery(id+"F43.wireOp",EDGE,"E96.0")}),-1.0]])]});
            extrude(context, id + "F44", {"entities" : qUnion([Q0, Q1]), "operationType" : NewBodyOperationType.ADD, "depth" : 5 * mm, "offsetDistance" : 25 * mm});
        }
        {
            var Q0;
            Q0=makeQuery(id+"F16.opExtrude","CAP_FACE",FACE,{"disambiguationData":[OSD([sQuery(id+"F15.wireOp",EDGE,"E57.bottom"),sQuery(id+"F15.wireOp",EDGE,"E57.top"),sQuery(id+"F15.wireOp",EDGE,"E57.left"),sQuery(id+"F15.wireOp",EDGE,"E57.right")])],"isStart":false});
            var sketch = newSketch(context, id + "F45", { "sketchPlane" : qUnion([Q0])});
            skCircle(sketch, "E98", {"center": v(0, 1300) * mm, "radius": 62.5 * mm});
            skSolve(sketch);
        }
        {
            var Q0;
            Q0=makeQuery(id+"F45.imprint","IMPRINT",FACE,{"disambiguationData":[TD([[makeQuery(id+"F45.imprint","IMPRINT",EDGE,{"derivedFrom":sQuery(id+"F45.wireOp",EDGE,"E98")}),1.0]])]});
            extrude(context, id + "F46", {"entities" : qUnion([Q0]), "operationType" : NewBodyOperationType.REMOVE, "oppositeDirection" : true, "depth" : 800 * mm, "offsetDistance" : 25 * mm});
        }
        {
            var Q0;
            Q0=makeQuery(id+"F10.opExtrude","SWEPT_FACE",FACE,{"disambiguationData":[OSD([sQuery(id+"F9.wireOp",EDGE,"E53.top")])]});
            var sketch = newSketch(context, id + "F47", { "sketchPlane" : qUnion([Q0])});
            skCircle(sketch, "E99", {"center": v(0, 1300) * mm, "radius": 75 * mm});
            skSolve(sketch);
        }
        {
            var Q0;
            Q0=makeQuery(id+"F47.imprint","IMPRINT",FACE,{"disambiguationData":[TD([[makeQuery(id+"F47.imprint","IMPRINT",EDGE,{"derivedFrom":sQuery(id+"F47.wireOp",EDGE,"E99")}),1.0]])]});
            extrude(context, id + "F48", {"entities" : qUnion([Q0]), "operationType" : NewBodyOperationType.ADD, "depth" : 100 * mm, "offsetDistance" : 25 * mm});
        }
        {
            var Q0;
            Q0=makeQuery(id+"F48.opExtrude","CAP_FACE",FACE,{"disambiguationData":[OSD([sQuery(id+"F9.wireOp",EDGE,"E53.top"),sQuery(id+"F45.wireOp",EDGE,"E98"),sQuery(id+"F47.wireOp",EDGE,"E99")])],"isStart":false});
            var sketch = newSketch(context, id + "F49", { "sketchPlane" : qUnion([Q0])});
            skCircle(sketch, "E100", {"center": v(0, 1300) * mm, "radius": 125 * mm});
            skCircle(sketch, "E101", {"center": v(0, 1405) * mm, "radius": 9 * mm});
            skCircle(sketch, "E102.1.0", {"center": v(-74.25, 1374.25) * mm, "radius": 9 * mm});
            skCircle(sketch, "E102.2.0", {"center": v(-105, 1300) * mm, "radius": 9 * mm});
            skCircle(sketch, "E102.3.0", {"center": v(-74.25, 1225.75) * mm, "radius": 9 * mm});
            skCircle(sketch, "E102.4.0", {"center": v(0, 1195) * mm, "radius": 9 * mm});
            skCircle(sketch, "E102.5.0", {"center": v(74.25, 1225.75) * mm, "radius": 9 * mm});
            skCircle(sketch, "E102.6.0", {"center": v(105, 1300) * mm, "radius": 9 * mm});
            skCircle(sketch, "E102.7.0", {"center": v(74.25, 1374.25) * mm, "radius": 9 * mm});
            skSolve(sketch);
        }
        {
            var Q0;
            Q0=makeQuery(id+"F49.imprint","IMPRINT",FACE,{"disambiguationData":[TD([[makeQuery(id+"F49.imprint","IMPRINT",EDGE,{"derivedFrom":sQuery(id+"F49.wireOp",EDGE,"E100")}),1.0]])]});
            var Q1;
            Q1=makeQuery(id+"F49.imprint","IMPRINT",FACE,{"disambiguationData":[TD([[makeQuery(id+"F49.imprint","IMPRINT",EDGE,{"derivedFrom":makeQuery(id+"F48.opExtrude","CAP_EDGE",EDGE,{"disambiguationData":[OSD([sQuery(id+"F47.wireOp",EDGE,"E99")])],"isStart":false})}),1.0]])]});
            extrude(context, id + "F50", {"entities" : qUnion([Q0, Q1]), "operationType" : NewBodyOperationType.ADD, "depth" : 25 * mm, "offsetDistance" : 25 * mm});
        }
        {
            var Q0;
            Q0=makeQuery(id+"F50.opExtrude","CAP_FACE",FACE,{"disambiguationData":[OSD([sQuery(id+"F9.wireOp",EDGE,"E53.top"),sQuery(id+"F45.wireOp",EDGE,"E98"),sQuery(id+"F49.wireOp",EDGE,"E100"),sQuery(id+"F49.wireOp",EDGE,"E101"),sQuery(id+"F49.wireOp",EDGE,"E102.1.0"),sQuery(id+"F49.wireOp",EDGE,"E102.2.0"),sQuery(id+"F49.wireOp",EDGE,"E102.3.0"),sQuery(id+"F49.wireOp",EDGE,"E102.4.0"),sQuery(id+"F49.wireOp",EDGE,"E102.5.0"),sQuery(id+"F49.wireOp",EDGE,"E102.6.0"),sQuery(id+"F49.wireOp",EDGE,"E102.7.0")])],"isStart":false});
            var sketch = newSketch(context, id + "F51", { "sketchPlane" : qUnion([Q0])});
            skCircle(sketch, "E103", {"center": v(0, 1300) * mm, "radius": 85 * mm});
            skSolve(sketch);
        }
        {
            var Q0;
            Q0=makeQuery(id+"F51.imprint","IMPRINT",FACE,{"disambiguationData":[TD([[makeQuery(id+"F51.imprint","IMPRINT",EDGE,{"derivedFrom":sQuery(id+"F51.wireOp",EDGE,"E103")}),1.0]])]});
            extrude(context, id + "F52", {"entities" : qUnion([Q0]), "operationType" : NewBodyOperationType.ADD, "depth" : 5 * mm, "offsetDistance" : 25 * mm});
        }
        {
            var Q0;
            Q0=makeQuery(id+"F14.boolean.opBoolean","MERGE",FACE,{"derivedFrom":[makeQuery(id+"F8.opExtrude","SWEPT_FACE",FACE,{"disambiguationData":[OSD([sQuery(id+"F7.wireOp",EDGE,"E52.trimOffspring")])]}),makeQuery(id+"F14.opExtrude","CAP_FACE",FACE,{"disambiguationData":[OSD([sQuery(id+"F13.wireOp",EDGE,"E55.bottom"),sQuery(id+"F13.wireOp",EDGE,"E55.top"),sQuery(id+"F13.wireOp",EDGE,"E55.left"),sQuery(id+"F13.wireOp",EDGE,"E55.right")])],"isStart":false})]});
            var sketch = newSketch(context, id + "F53", { "sketchPlane" : qUnion([Q0])});
            skCircle(sketch, "E104", {"center": v(-600, 1379.34) * mm, "radius": 50 * mm});
            skCircle(sketch, "E105", {"center": v(-600, 1179.34) * mm, "radius": 50 * mm});
            skCircle(sketch, "E106.MirrorC", {"center": v(600, 1379.34) * mm, "radius": 50 * mm});
            skCircle(sketch, "E107.MirrorC", {"center": v(600, 1179.34) * mm, "radius": 50 * mm});
            skSolve(sketch);
        }
        {
            var Q0;
            Q0 = qSketchRegion(id + "F53", true);
            extrude(context, id + "F54", {"entities" : qUnion([Q0]), "operationType" : NewBodyOperationType.ADD, "depth" : 700 * mm, "offsetDistance" : 25 * mm});
        }
        {
            var Q0;
            Q0=makeQuery(id+"F54.opExtrude","CAP_FACE",FACE,{"disambiguationData":[OSD([sQuery(id+"F53.wireOp",EDGE,"E104")])],"isStart":false});
            var sketch = newSketch(context, id + "F55", { "sketchPlane" : qUnion([Q0])});
            skLineSegment(sketch, "E108.bottom", {"start": v(-700, 1429.34) * mm, "end": v(700, 1429.34) * mm});
            skLineSegment(sketch, "E108.top", {"start": v(-700, 1129.34) * mm, "end": v(700, 1129.34) * mm});
            skLineSegment(sketch, "E108.left", {"start": v(-700, 1429.34) * mm, "end": v(-700, 1129.34) * mm});
            skLineSegment(sketch, "E108.right", {"start": v(700, 1429.34) * mm, "end": v(700, 1129.34) * mm});
            skSolve(sketch);
        }
        {
            var Q0;
            Q0 = qSketchRegion(id + "F55", true);
            extrude(context, id + "F56", {"entities" : qUnion([Q0]), "operationType" : NewBodyOperationType.ADD, "depth" : 184 * mm, "offsetDistance" : 25 * mm});
        }
        {
            var Q0;
            Q0=makeQuery(id+"F4.opExtrude","SWEPT_FACE",FACE,{"disambiguationData":[OSD([sQuery(id+"F3.wireOp",EDGE,"E38.MirrorCS")])]});
            var sketch = newSketch(context, id + "F57", { "sketchPlane" : qUnion([Q0])});
            skLineSegment(sketch, "E109", {"start": v(520, 420) * mm, "end": v(620, 420) * mm});
            skLineSegment(sketch, "E110", {"start": v(640, 400) * mm, "end": v(640, 350) * mm});
            skLineSegment(sketch, "E111", {"start": v(625.6, 330.8) * mm, "end": v(520, 300) * mm});
            skPoint(sketch, "E112.visualSharp", {"position": v(640, 420) * mm});
            skArc(sketch, "E112.filletArc", {"start": v(640, 400) * mm, "mid": v(634.14, 414.14) * mm, "end": v(620, 420) * mm});
            skPoint(sketch, "E113.visualSharp", {"position": v(640, 335) * mm});
            skArc(sketch, "E113.filletArc", {"start": v(625.6, 330.8) * mm, "mid": v(636, 338) * mm, "end": v(640, 350) * mm});
            skLineSegment(sketch, "E114.0", {"start": v(-520, 1040) * mm, "end": v(-520, 20) * mm});
            skLineSegment(sketch, "E115", {"start": v(-520, 420) * mm, "end": v(-620, 420) * mm});
            skLineSegment(sketch, "E116", {"start": v(-640, 400) * mm, "end": v(-640, 358.54) * mm});
            skLineSegment(sketch, "E117", {"start": v(-626.97, 339.8) * mm, "end": v(-520, 300) * mm});
            skPoint(sketch, "E118.visualSharp", {"position": v(-640, 420) * mm});
            skArc(sketch, "E118.filletArc", {"start": v(-620, 420) * mm, "mid": v(-634.14, 414.14) * mm, "end": v(-640, 400) * mm});
            skPoint(sketch, "E119.visualSharp", {"position": v(-640, 344.64) * mm});
            skArc(sketch, "E119.filletArc", {"start": v(-640, 358.54) * mm, "mid": v(-636.42, 347.13) * mm, "end": v(-626.97, 339.8) * mm});
            skSolve(sketch);
        }
        {
            var Q0;
            Q0 = qSketchRegion(id + "F57", true);
            var Q1;
            {var subQ1=sQuery(id+"F57.wireOp",EDGE,"E109");Q1=makeQuery(id+"F57.imprint","IMPRINT",FACE,{"disambiguationData":[TD([[makeQuery(id+"F57.imprint","IMPRINT",EDGE,{"derivedFrom":subQ1}),-1.0]])]});}
            extrude(context, id + "F58", {"entities" : qUnion([Q0, Q1]), "operationType" : NewBodyOperationType.ADD, "oppositeDirection" : true, "depth" : 40 * mm, "offsetDistance" : 25 * mm});
        }
        {
            var Q0;
            Q0=makeQuery(id+"F58.boolean.opBoolean","MERGE",FACE,{"derivedFrom":[makeQuery(id+"F4.opExtrude","SWEPT_FACE",FACE,{"disambiguationData":[OSD([sQuery(id+"F3.wireOp",EDGE,"E37.bottom")])]}),makeQuery(id+"F58.opExtrude","CAP_FACE",FACE,{"disambiguationData":[OSD([sQuery(id+"F57.wireOp",EDGE,"E114.0"),sQuery(id+"F57.wireOp",EDGE,"E115"),sQuery(id+"F57.wireOp",EDGE,"E116"),sQuery(id+"F57.wireOp",EDGE,"E117"),sQuery(id+"F57.wireOp",EDGE,"E118.filletArc"),sQuery(id+"F57.wireOp",EDGE,"E119.filletArc")])],"isStart":true})]});
            var sketch = newSketch(context, id + "F59", { "sketchPlane" : qUnion([Q0])});
            skLineSegment(sketch, "E120", {"start": v(-596.04, 479.14) * mm, "end": v(-654.32, 239.88) * mm});
            skLineSegment(sketch, "E121", {"start": v(-654.32, 239.88) * mm, "end": v(-538.78, 176.67) * mm});
            skLineSegment(sketch, "E122", {"start": v(-538.78, 176.67) * mm, "end": v(-438.08, 360.72) * mm});
            skLineSegment(sketch, "E123", {"start": v(-438.08, 360.72) * mm, "end": v(-596.04, 479.14) * mm});
            skLineSegment(sketch, "E124", {"start": v(402.57, 479.14) * mm, "end": v(483.87, 479.14) * mm});
            skLineSegment(sketch, "E125", {"start": v(483.87, 479.14) * mm, "end": v(670.96, 300) * mm});
            skLineSegment(sketch, "E126", {"start": v(670.96, 300) * mm, "end": v(613.4, 239.88) * mm});
            skLineSegment(sketch, "E127", {"start": v(613.4, 239.88) * mm, "end": v(425.29, 420) * mm});
            skLineSegment(sketch, "E128", {"start": v(425.29, 420) * mm, "end": v(402.57, 479.14) * mm});
            skSolve(sketch);
        }
        {
            var Q0;
            Q0=makeQuery(id+"F6.opExtrude","SWEPT_FACE",FACE,{"disambiguationData":[OSD([sQuery(id+"F5.wireOp",EDGE,"E44.MirrorCS")])]});
            var sketch = newSketch(context, id + "F60", { "sketchPlane" : qUnion([Q0])});
            skLineSegment(sketch, "E129.bottom", {"start": v(-420, 420) * mm, "end": v(-617.72, 420) * mm});
            skLineSegment(sketch, "E129.top", {"start": v(-420, 345) * mm, "end": v(-617.72, 345) * mm});
            skLineSegment(sketch, "E129.left", {"start": v(-420, 420) * mm, "end": v(-420, 345) * mm});
            skLineSegment(sketch, "E129.right", {"start": v(-637.72, 400) * mm, "end": v(-637.72, 365) * mm});
            skLineSegment(sketch, "E130.bottom", {"start": v(420, 345) * mm, "end": v(620, 345) * mm});
            skLineSegment(sketch, "E130.top", {"start": v(420, 420) * mm, "end": v(620, 420) * mm});
            skLineSegment(sketch, "E130.left", {"start": v(420, 345) * mm, "end": v(420, 420) * mm});
            skLineSegment(sketch, "E130.right", {"start": v(640, 365) * mm, "end": v(640, 400) * mm});
            skPoint(sketch, "E131.visualSharp", {"position": v(640, 420) * mm});
            skArc(sketch, "E131.filletArc", {"start": v(640, 400) * mm, "mid": v(634.14, 414.14) * mm, "end": v(620, 420) * mm});
            skPoint(sketch, "E132.visualSharp", {"position": v(640, 345) * mm});
            skArc(sketch, "E132.filletArc", {"start": v(620, 345) * mm, "mid": v(634.14, 350.86) * mm, "end": v(640, 365) * mm});
            skPoint(sketch, "E133.visualSharp", {"position": v(-637.72, 420) * mm});
            skArc(sketch, "E133.filletArc", {"start": v(-617.72, 420) * mm, "mid": v(-631.86, 414.14) * mm, "end": v(-637.72, 400) * mm});
            skPoint(sketch, "E134.visualSharp", {"position": v(-637.72, 345) * mm});
            skArc(sketch, "E134.filletArc", {"start": v(-637.72, 365) * mm, "mid": v(-631.86, 350.86) * mm, "end": v(-617.72, 345) * mm});
            skSolve(sketch);
        }
        {
            var Q0;
            Q0 = qSketchRegion(id + "F60", true);
            extrude(context, id + "F61", {"entities" : qUnion([Q0]), "operationType" : NewBodyOperationType.ADD, "oppositeDirection" : true, "depth" : 25 * mm, "offsetDistance" : 25 * mm});
        }
        {
            var Q0;
            Q0=makeQuery(id+"F2.opExtrude","CAP_FACE",FACE,{"disambiguationData":[OSD([sQuery(id+"F0.wireOp",EDGE,"E5.MirrorCS"),sQuery(id+"F0.wireOp",EDGE,"E6.MirrorCS"),sQuery(id+"F0.wireOp",EDGE,"E7.MirrorCS"),sQuery(id+"F0.wireOp",EDGE,"E8.MirrorCS"),sQuery(id+"F0.wireOp",EDGE,"E10.MirrorCS"),sQuery(id+"F0.wireOp",EDGE,"E13.MirrorCS"),sQuery(id+"F0.wireOp",EDGE,"E15.MirrorCS"),sQuery(id+"F0.wireOp",EDGE,"E16.MirrorCS")])],"isStart":true});
            cPlane(context, id + "F62", {"entities" : qUnion([Q0]), "cplaneType" : CPlaneType.OFFSET, "offset" : 350 * mm, "oppositeDirection" : true, "width" : 150 * mm, "height" : 150 * mm});
        }
        {
            var Q0;
            Q0=qCreatedBy(id+"F62.planeOp",FACE);
            var sketch = newSketch(context, id + "F63", { "sketchPlane" : qUnion([Q0])});
            skLineSegment(sketch, "E135.bottom", {"start": v(-602.8, 759.48) * mm, "end": v(579.12, 759.48) * mm});
            skLineSegment(sketch, "E135.top", {"start": v(-602.8, 259.48) * mm, "end": v(579.12, 259.48) * mm});
            skLineSegment(sketch, "E135.left", {"start": v(-602.8, 759.48) * mm, "end": v(-602.8, 259.48) * mm});
            skLineSegment(sketch, "E135.right", {"start": v(579.12, 759.48) * mm, "end": v(579.12, 259.48) * mm});
            skSolve(sketch);
        }
        {
            var Q0;
            Q0 = qSketchRegion(id + "F63", true);
            extrude(context, id + "F64", {"entities" : qUnion([Q0]), "operationType" : NewBodyOperationType.ADD, "depth" : 25 * mm, "offsetDistance" : 25 * mm});
        }
        {
            var Q0;
            Q0=makeQuery(id+"F64.opExtrude","CAP_FACE",FACE,{"disambiguationData":[OSD([sQuery(id+"F63.wireOp",EDGE,"E135.bottom"),sQuery(id+"F63.wireOp",EDGE,"E135.top"),sQuery(id+"F63.wireOp",EDGE,"E135.left"),sQuery(id+"F63.wireOp",EDGE,"E135.right")])],"isStart":false});
            var sketch = newSketch(context, id + "F65", { "sketchPlane" : qUnion([Q0])});
            skCircle(sketch, "E136", {"center": v(0, 556.09) * mm, "radius": 100 * mm});
            skCircle(sketch, "E137", {"center": v(0, 556.09) * mm, "radius": 110 * mm});
            skLineSegment(sketch, "E138.0.0", {"start": v(543.46, 156.09) * mm, "end": v(613.4, 156.09) * mm});
            skLineSegment(sketch, "E138.0.1", {"start": v(613.4, 156.09) * mm, "end": v(613.4, 9356.09) * mm});
            skLineSegment(sketch, "E138.0.2", {"start": v(613.4, 9356.09) * mm, "end": v(425.29, 9356.09) * mm});
            skLineSegment(sketch, "E138.0.3", {"start": v(425.29, 9356.09) * mm, "end": v(425.29, 156.09) * mm});
            skLineSegment(sketch, "E138.0.4", {"start": v(425.29, 156.09) * mm, "end": v(543.46, 156.09) * mm});
            skSolve(sketch);
        }
        {
            var Q0;
            Q0=makeQuery(id+"F65.imprint","IMPRINT",FACE,{"disambiguationData":[TD([[makeQuery(id+"F65.imprint","IMPRINT",EDGE,{"derivedFrom":sQuery(id+"F65.wireOp",EDGE,"E136")}),-1.0]])]});
            extrude(context, id + "F66", {"entities" : qUnion([Q0]), "operationType" : NewBodyOperationType.ADD, "depth" : 50 * mm, "offsetDistance" : 25 * mm});
        }
    });
